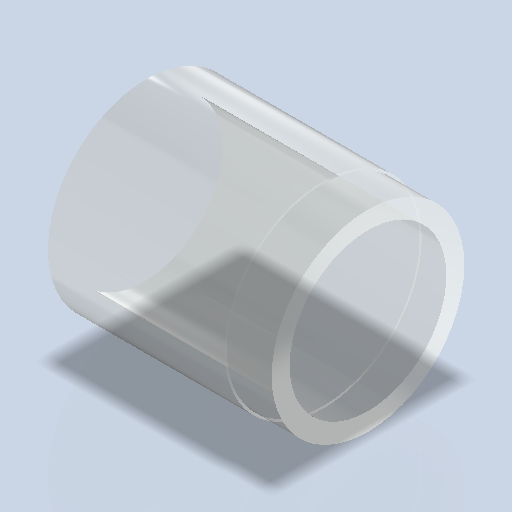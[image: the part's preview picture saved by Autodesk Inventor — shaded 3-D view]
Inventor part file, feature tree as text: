
AUTODESK INVENTOR PART (.ipt)
format: ipt  version: 2024 (Build 280153000, 153)  size: 353,280 bytes
history: native  units: mm
features: sketch x2, revolve x1, chamfer x1, extrude x1
ambient origin geometry x8: Origin, YZ Plane, XZ Plane, XY Plane, X Axis, Y Axis, Z Axis, Center Point
bodies: Volumenkörper1 (feature_tree)
feature tree (5):
  revolve  "Umdrehung1"
  chamfer  "Fasen1"  Distance=40.0mm
  extrude  "Extrusion1"  Depth=50.0mm
  sketch  "Skizze1"  dims[d0=44.0mm]
  sketch  "Skizze2"  dims[d1=43.0mm d2=40.0mm d3=50.0mm d4=90.0deg d5=2.0mm d6=2.0mm d7=15.0deg d8=35.0mm d9=10.0mm d10=0.0mm]
